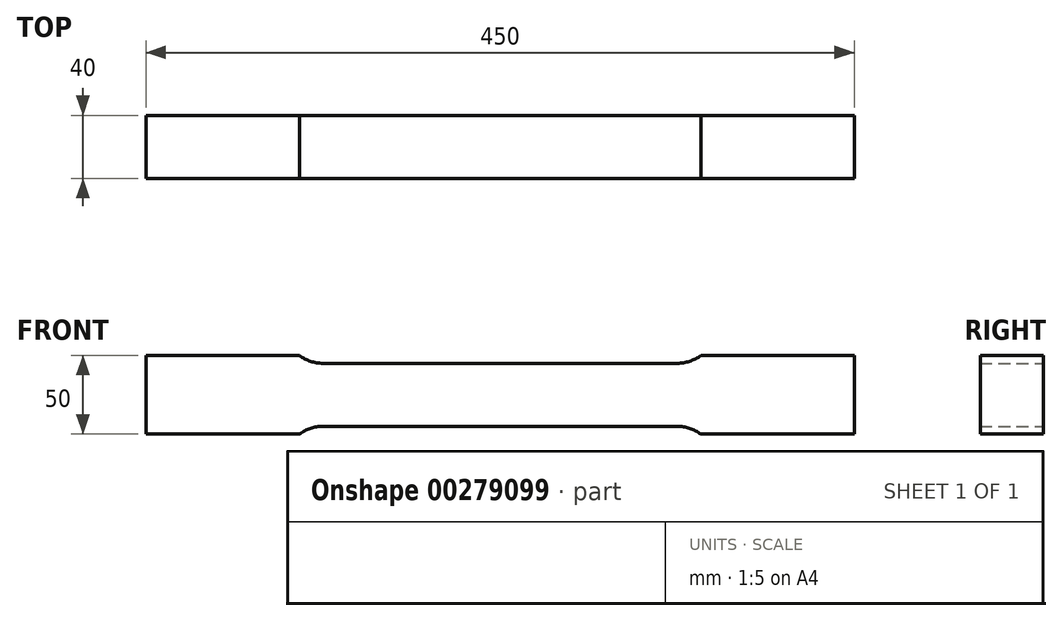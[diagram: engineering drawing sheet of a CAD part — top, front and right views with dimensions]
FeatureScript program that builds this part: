
annotation { "Feature Type Name" : "Feature", "Feature Type Description" : "" }
export const myFeature = defineFeature(function(context is Context, id is Id, definition is map)
    precondition{}
    {
        {
            var Q0;
            Q0=qCreatedBy(makeId("Front.planeOp"),FACE);
            var sketch = newSketch(context, id + "F0", { "sketchPlane" : qUnion([Q0])});
            skLineSegment(sketch, "E0", {"start": v(0, 20) * mm, "end": v(112.5, 20) * mm});
            skArc(sketch, "E1", {"start": v(112.5, 20) * mm, "mid": v(120.4, 21.28) * mm, "end": v(127.5, 25) * mm});
            skLineSegment(sketch, "E2", {"start": v(127.5, 25) * mm, "end": v(225, 25) * mm});
            skLineSegment(sketch, "E3.MirrorCS", {"start": v(127.5, -25) * mm, "end": v(225, -25) * mm});
            skLineSegment(sketch, "E4.MirrorCS", {"start": v(0, -20) * mm, "end": v(112.5, -20) * mm});
            skArc(sketch, "E5.MirrorCS", {"start": v(112.5, -20) * mm, "mid": v(120.4, -21.28) * mm, "end": v(127.5, -25) * mm});
            skLineSegment(sketch, "E6.MirrorCS", {"start": v(0, 20) * mm, "end": v(-112.5, 20) * mm});
            skArc(sketch, "E7.MirrorCS", {"start": v(-112.5, 20) * mm, "mid": v(-120.4, 21.28) * mm, "end": v(-127.5, 25) * mm});
            skLineSegment(sketch, "E8.MirrorCS", {"start": v(-127.5, 25) * mm, "end": v(-225, 25) * mm});
            skLineSegment(sketch, "E9.MirrorCS", {"start": v(-127.5, -25) * mm, "end": v(-225, -25) * mm});
            skArc(sketch, "E10.MirrorCS", {"start": v(-112.5, -20) * mm, "mid": v(-120.4, -21.28) * mm, "end": v(-127.5, -25) * mm});
            skLineSegment(sketch, "E11.MirrorCS", {"start": v(0, -20) * mm, "end": v(-112.5, -20) * mm});
            skLineSegment(sketch, "E12", {"start": v(-225, 25) * mm, "end": v(-225, -25) * mm});
            skLineSegment(sketch, "E13", {"start": v(225, 25) * mm, "end": v(225, -25) * mm});
            skSolve(sketch);
        }
        {
            var Q0;
            Q0=makeQuery(id+"F0.imprint","IMPRINT",FACE,{"disambiguationData":[TD([[makeQuery(id+"F0.imprint","IMPRINT",EDGE,{"derivedFrom":sQuery(id+"F0.wireOp",EDGE,"E1")}),-1.0]])]});
            extrude(context, id + "F1", {"entities" : qUnion([Q0]), "endBound" : BoundingType.SYMMETRIC, "depth" : 40 * mm});
        }
    });
